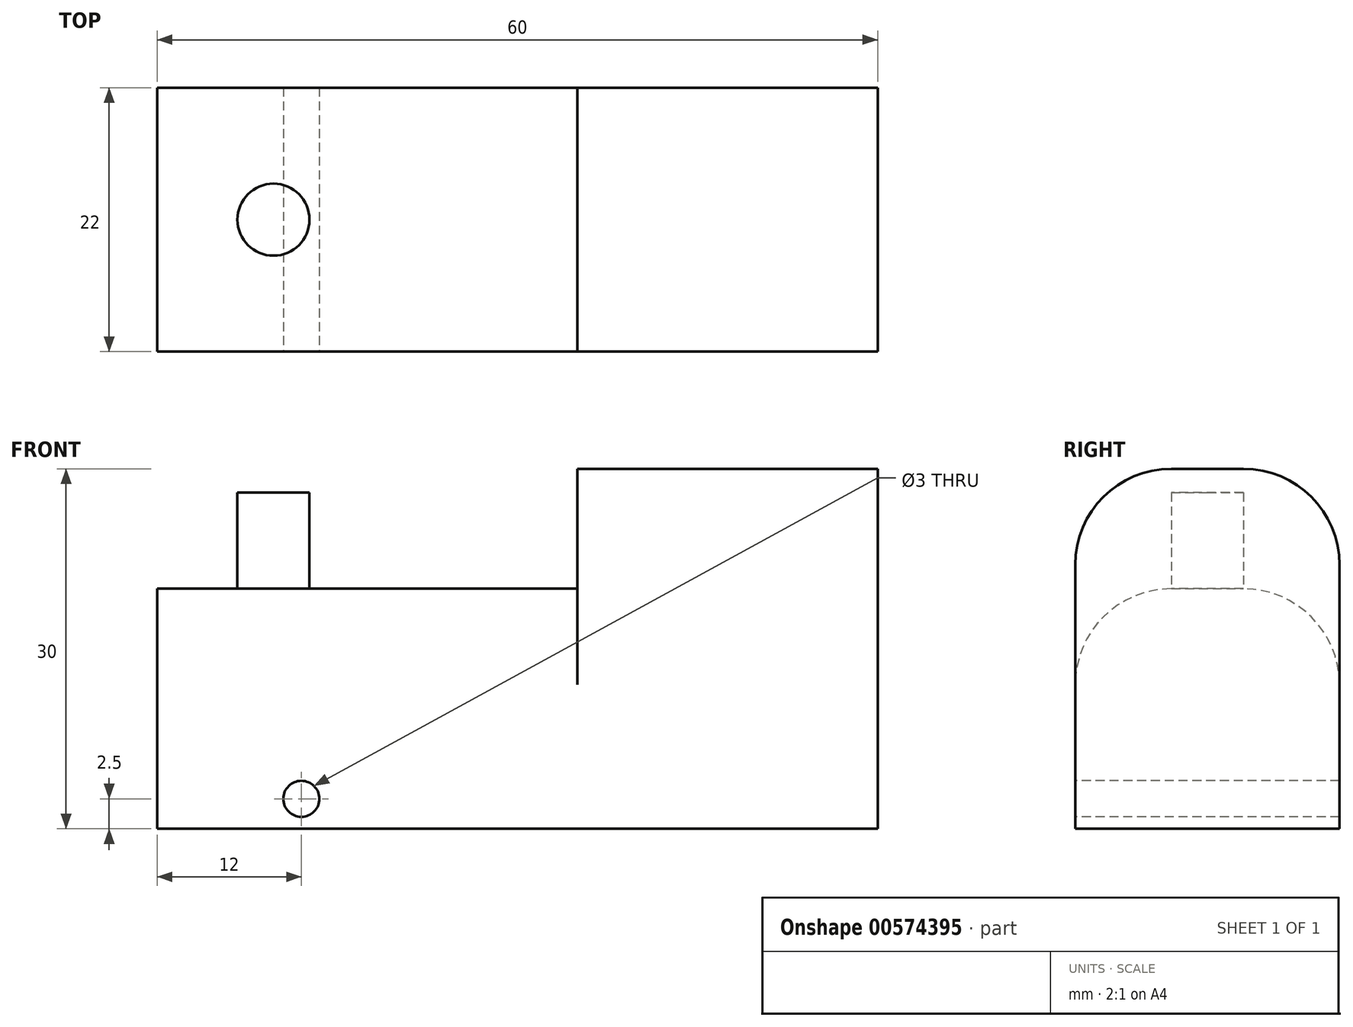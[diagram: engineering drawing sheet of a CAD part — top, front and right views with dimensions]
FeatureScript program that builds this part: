
annotation { "Feature Type Name" : "Feature", "Feature Type Description" : "" }
export const myFeature = defineFeature(function(context is Context, id is Id, definition is map)
    precondition{}
    {
        {
            var Q0;
            Q0=qCreatedBy(makeId("Front.planeOp"),FACE);
            var sketch = newSketch(context, id + "F0", { "sketchPlane" : qUnion([Q0])});
            skLineSegment(sketch, "E0.bottom", {"start": v(0, 0) * mm, "end": v(60, 0) * mm});
            skLineSegment(sketch, "E0.top", {"start": v(0, 20) * mm, "end": v(60, 20) * mm});
            skLineSegment(sketch, "E0.left", {"start": v(0, 0) * mm, "end": v(0, 20) * mm});
            skLineSegment(sketch, "E0.right", {"start": v(60, 0) * mm, "end": v(60, 20) * mm});
            skLineSegment(sketch, "E1", {"start": v(35, 0) * mm, "end": v(35, 20) * mm});
            skLineSegment(sketch, "E2", {"start": v(35, 20) * mm, "end": v(35, 30) * mm});
            skLineSegment(sketch, "E3", {"start": v(35, 30) * mm, "end": v(60, 30) * mm});
            skLineSegment(sketch, "E4", {"start": v(60, 30) * mm, "end": v(60, 20) * mm});
            skSolve(sketch);
        }
        {
            var Q0;
            {var subQ0=sQuery(id+"F0.wireOp",EDGE,"E0.left");Q0=makeQuery(id+"F0.imprint","IMPRINT",FACE,{"disambiguationData":[TD([[makeQuery(id+"F0.imprint","IMPRINT",EDGE,{"derivedFrom":subQ0}),-1.0]])]});}
            var Q1;
            {var subQ0=sQuery(id+"F0.wireOp",EDGE,"E0.right");Q1=makeQuery(id+"F0.imprint","IMPRINT",FACE,{"disambiguationData":[TD([[makeQuery(id+"F0.imprint","IMPRINT",EDGE,{"derivedFrom":subQ0}),1.0]])]});}
            var Q2;
            {var subQ2=sQuery(id+"F0.wireOp",EDGE,"E2");Q2=makeQuery(id+"F0.imprint","IMPRINT",FACE,{"disambiguationData":[TD([[makeQuery(id+"F0.imprint","IMPRINT",EDGE,{"derivedFrom":subQ2}),-1.0]])]});}
            extrude(context, id + "F1", {"entities" : qUnion([Q0, Q1, Q2]), "endBound" : BoundingType.SYMMETRIC, "depth" : 22 * mm, "offsetDistance" : 25 * mm});
        }
        {
            var Q0;
            Q0=makeQuery(id+"F1.opExtrude","CAP_EDGE",EDGE,{"disambiguationData":[OSD([sQuery(id+"F0.wireOp",EDGE,"E0.top")])],"isStart":false});
            var Q1;
            Q1=makeQuery(id+"F1.opExtrude","CAP_EDGE",EDGE,{"disambiguationData":[OSD([sQuery(id+"F0.wireOp",EDGE,"E0.top")])],"isStart":true});
            fillet(context, id + "F2", {"entities" : qUnion([Q0, Q1]), "radius" : 8 * mm, "tangentPropagation" : true, "allowEdgeOverflow" : false});
        }
        {
            var Q0;
            Q0=makeQuery(id+"F1.opExtrude","CAP_EDGE",EDGE,{"disambiguationData":[OSD([sQuery(id+"F0.wireOp",EDGE,"E3")])],"isStart":false});
            var Q1;
            Q1=makeQuery(id+"F1.opExtrude","CAP_EDGE",EDGE,{"disambiguationData":[OSD([sQuery(id+"F0.wireOp",EDGE,"E3")])],"isStart":true});
            fillet(context, id + "F3", {"entities" : qUnion([Q0, Q1]), "radius" : 8 * mm, "tangentPropagation" : true, "allowEdgeOverflow" : false});
        }
        {
            var Q0;
            Q0=makeQuery(id+"F1.opExtrude","SWEPT_FACE",FACE,{"disambiguationData":[OSD([sQuery(id+"F0.wireOp",EDGE,"E0.top")])]});
            var sketch = newSketch(context, id + "F4", { "sketchPlane" : qUnion([Q0])});
            skCircle(sketch, "E5", {"center": v(9.68, 0) * mm, "radius": 3 * mm});
            skSolve(sketch);
        }
        {
            var Q0;
            {var subQ0=sQuery(id+"F4.wireOp",EDGE,"E5");var subQ1=sQuery(id+"F0.wireOp",EDGE,"E0.top");var subQ2=makeQuery(id+"F1.opExtrude","SWEPT_FACE",FACE,{"disambiguationData":[OSD([subQ1])]});var subQ3=makeQuery(id+"F4.imprint","INTERSECT",VERTEX,{"derivedFrom":[makeQuery(id+"F2.opFillet","BLEND_EDGE",EDGE,{"blendedFrom":[makeQuery(id+"F1.opExtrude","CAP_EDGE",EDGE,{"disambiguationData":[OSD([subQ1])],"isStart":true}),subQ2],"blendedInto":[subQ2]}),subQ0]});Q0=makeQuery(id+"F4.imprint","IMPRINT",FACE,{"disambiguationData":[TD([[makeQuery(id+"F4.imprint","IMPRINT",EDGE,{"disambiguationData":[TD([[subQ3,-1.0]])],"derivedFrom":subQ0}),1.0]])]});}
            extrude(context, id + "F5", {"entities" : qUnion([Q0]), "operationType" : NewBodyOperationType.ADD, "depth" : 8 * mm, "offsetDistance" : 25 * mm});
        }
        {
            var Q0;
            Q0=qCreatedBy(makeId("Front.planeOp"),FACE);
            var sketch = newSketch(context, id + "F6", { "sketchPlane" : qUnion([Q0])});
            skCircle(sketch, "E6", {"center": v(12, 2.5) * mm, "radius": 1.5 * mm});
            skSolve(sketch);
        }
        {
            var Q0;
            Q0 = qSketchRegion(id + "F6", true);
            extrude(context, id + "F7", {"entities" : qUnion([Q0]), "operationType" : NewBodyOperationType.REMOVE, "endBound" : BoundingType.SYMMETRIC, "oppositeDirection" : true, "depth" : 25 * mm, "offsetDistance" : 25 * mm});
        }
        {
            var Q0;
            Q0=qCreatedBy(makeId("Right.planeOp"),FACE);
            cPlane(context, id + "F8", {"entities" : qUnion([Q0]), "cplaneType" : CPlaneType.OFFSET, "offset" : 30 * mm, "width" : 150 * mm, "height" : 150 * mm});
        }
    });
